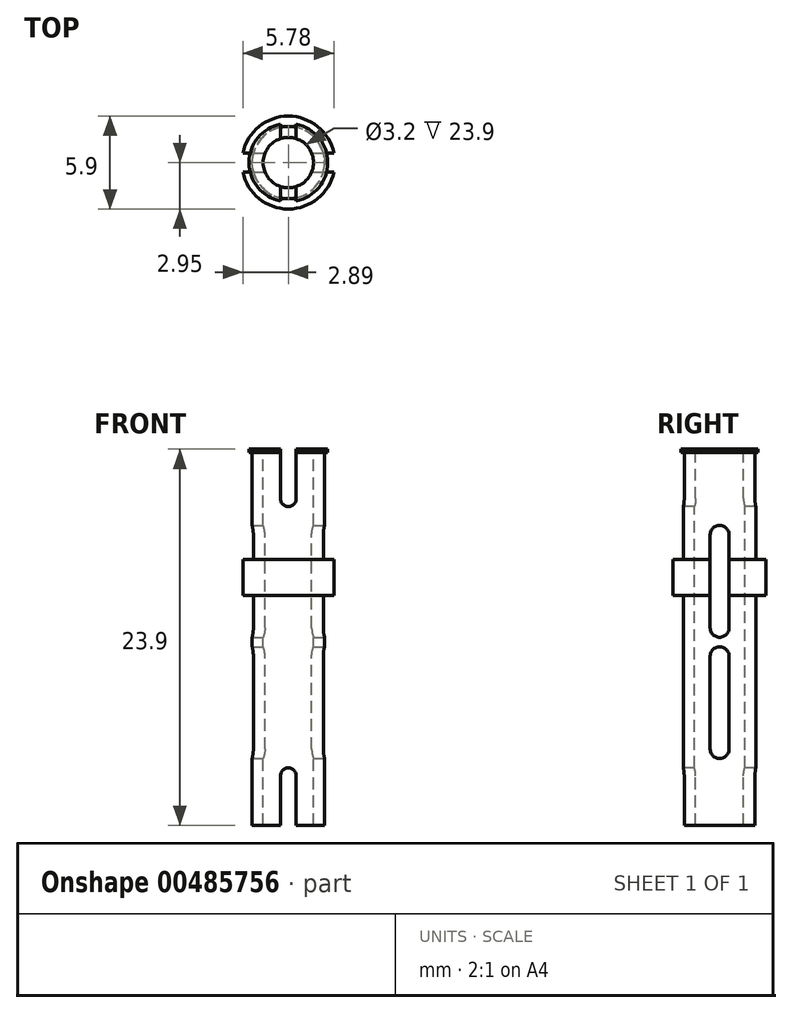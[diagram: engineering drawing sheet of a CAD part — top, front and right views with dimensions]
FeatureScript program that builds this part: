
annotation { "Feature Type Name" : "Feature", "Feature Type Description" : "" }
export const myFeature = defineFeature(function(context is Context, id is Id, definition is map)
    precondition{}
    {
        {
            var Q0;
            Q0=qCreatedBy(makeId("Top.planeOp"),FACE);
            var sketch = newSketch(context, id + "F0", { "sketchPlane" : qUnion([Q0])});
            skCircle(sketch, "E0", {"center": v(0, 0) * mm, "radius": 2.95 * mm});
            skSolve(sketch);
        }
        {
            var Q0;
            Q0 = qSketchRegion(id + "F0", true);
            extrude(context, id + "F1", {"entities" : qUnion([Q0]), "endBound" : BoundingType.SYMMETRIC, "depth" : 23.9 * mm, "offsetDistance" : 25 * mm});
        }
        {
            var Q0;
            Q0=makeQuery(id+"F1.opExtrude","CAP_FACE",FACE,{"disambiguationData":[OSD([sQuery(id+"F0.wireOp",EDGE,"E0")])],"isStart":false});
            var sketch = newSketch(context, id + "F2", { "sketchPlane" : qUnion([Q0])});
            skCircle(sketch, "E1", {"center": v(0, 0) * mm, "radius": 2.3 * mm});
            skSolve(sketch);
        }
        {
            var Q0;
            Q0=makeQuery(id+"F2.imprint","IMPRINT",FACE,{"disambiguationData":[TD([[makeQuery(id+"F2.imprint","IMPRINT",EDGE,{"derivedFrom":sQuery(id+"F2.wireOp",EDGE,"E1")}),-1.0]])]});
            extrude(context, id + "F3", {"entities" : qUnion([Q0]), "operationType" : NewBodyOperationType.REMOVE, "oppositeDirection" : true, "depth" : 7 * mm, "offsetDistance" : 25 * mm});
        }
        {
            var Q0;
            Q0=makeQuery(id+"F1.opExtrude","CAP_FACE",FACE,{"disambiguationData":[OSD([sQuery(id+"F0.wireOp",EDGE,"E0")])],"isStart":true});
            var sketch = newSketch(context, id + "F4", { "sketchPlane" : qUnion([Q0])});
            skCircle(sketch, "E2", {"center": v(0, 0) * mm, "radius": 2.3 * mm});
            skSolve(sketch);
        }
        {
            var Q0;
            Q0=makeQuery(id+"F4.imprint","IMPRINT",FACE,{"disambiguationData":[TD([[makeQuery(id+"F4.imprint","IMPRINT",EDGE,{"derivedFrom":sQuery(id+"F4.wireOp",EDGE,"E2")}),-1.0]])]});
            extrude(context, id + "F5", {"entities" : qUnion([Q0]), "operationType" : NewBodyOperationType.REMOVE, "oppositeDirection" : true, "depth" : 14.6 * mm, "offsetDistance" : 25 * mm});
        }
        {
            var Q0;
            Q0=makeQuery(id+"F1.opExtrude","CAP_FACE",FACE,{"disambiguationData":[OSD([sQuery(id+"F0.wireOp",EDGE,"E0")])],"isStart":false});
            var sketch = newSketch(context, id + "F6", { "sketchPlane" : qUnion([Q0])});
            skCircle(sketch, "E3", {"center": v(0, 0) * mm, "radius": 1.6 * mm});
            skSolve(sketch);
        }
        {
            var Q0;
            Q0 = qSketchRegion(id + "F6", true);
            extrude(context, id + "F7", {"entities" : qUnion([Q0]), "operationType" : NewBodyOperationType.REMOVE, "endBound" : BoundingType.THROUGH_ALL, "oppositeDirection" : true, "depth" : 25 * mm, "offsetDistance" : 25 * mm});
        }
        {
            var Q0;
            Q0=qCreatedBy(makeId("Front.planeOp"),FACE);
            var sketch = newSketch(context, id + "F8", { "sketchPlane" : qUnion([Q0])});
            skLineSegment(sketch, "E4.bottom", {"start": v(-0.5, 8.8) * mm, "end": v(0.5, 8.8) * mm});
            skLineSegment(sketch, "E4.top", {"start": v(-0.5, 11.95) * mm, "end": v(0.5, 11.95) * mm});
            skLineSegment(sketch, "E4.left", {"start": v(-0.5, 8.8) * mm, "end": v(-0.5, 11.95) * mm});
            skLineSegment(sketch, "E4.right", {"start": v(0.5, 8.8) * mm, "end": v(0.5, 11.95) * mm});
            skPoint(sketch, "E4.middle", {"position": v(0, 10.38) * mm});
            skCircle(sketch, "E5", {"center": v(0, 8.8) * mm, "radius": 0.5 * mm});
            skLineSegment(sketch, "E6.bottom", {"start": v(-0.5, -11.95) * mm, "end": v(0.5, -11.95) * mm});
            skLineSegment(sketch, "E6.top", {"start": v(-0.5, -8.8) * mm, "end": v(0.5, -8.8) * mm});
            skLineSegment(sketch, "E6.left", {"start": v(-0.5, -11.95) * mm, "end": v(-0.5, -8.8) * mm});
            skLineSegment(sketch, "E6.right", {"start": v(0.5, -11.95) * mm, "end": v(0.5, -8.8) * mm});
            skPoint(sketch, "E6.middle", {"position": v(0, -10.38) * mm});
            skCircle(sketch, "E7", {"center": v(0, -8.8) * mm, "radius": 0.5 * mm});
            skSolve(sketch);
        }
        {
            var Q0;
            Q0 = qSketchRegion(id + "F8", true);
            extrude(context, id + "F9", {"entities" : qUnion([Q0]), "operationType" : NewBodyOperationType.REMOVE, "endBound" : BoundingType.SYMMETRIC, "oppositeDirection" : true, "depth" : 25 * mm, "offsetDistance" : 25 * mm});
        }
        {
            var Q0;
            Q0=qCreatedBy(makeId("Front.planeOp"),FACE);
            var sketch = newSketch(context, id + "F10", { "sketchPlane" : qUnion([Q0])});
            skLineSegment(sketch, "E8.bottom", {"start": v(2.3, 11.95) * mm, "end": v(2.5, 11.95) * mm});
            skLineSegment(sketch, "E8.top", {"start": v(2.3, 11.75) * mm, "end": v(2.5, 11.75) * mm});
            skLineSegment(sketch, "E8.left", {"start": v(2.3, 11.95) * mm, "end": v(2.3, 11.75) * mm});
            skLineSegment(sketch, "E8.right", {"start": v(2.5, 11.95) * mm, "end": v(2.5, 11.75) * mm});
            skSolve(sketch);
        }
        {
            var Q0;
            Q0 = qSketchRegion(id + "F10", true);
            var Q1;
            Q1=makeQuery(id+"F3.boolean.opBoolean","COPY",FACE,{"derivedFrom":makeQuery(id+"F3.opExtrude","SWEPT_FACE",FACE,{"disambiguationData":[OSD([sQuery(id+"F2.wireOp",EDGE,"E1")])]})});
            revolve(context, id + "F11", {"operationType" : NewBodyOperationType.ADD, "entities" : qUnion([Q0]), "axis" : qUnion([Q1]), "revolveType" : RevolveType.FULL});
        }
        {
            var Q0;
            Q0 = qSketchRegion(id + "F8", true);
            extrude(context, id + "F12", {"entities" : qUnion([Q0]), "operationType" : NewBodyOperationType.REMOVE, "endBound" : BoundingType.SYMMETRIC, "depth" : 25 * mm, "offsetDistance" : 25 * mm});
        }
        {
            var Q0;
            Q0 = qSketchRegion(id + "F8", true);
            extrude(context, id + "F13", {"entities" : qUnion([Q0]), "operationType" : NewBodyOperationType.REMOVE, "endBound" : BoundingType.SYMMETRIC, "oppositeDirection" : true, "depth" : 25 * mm, "offsetDistance" : 25 * mm});
        }
        {
            var Q0;
            Q0=qCreatedBy(makeId("Right.planeOp"),FACE);
            var sketch = newSketch(context, id + "F14", { "sketchPlane" : qUnion([Q0])});
            skLineSegment(sketch, "E9.bottom", {"start": v(0.6, 0.6) * mm, "end": v(-0.6, 0.6) * mm});
            skLineSegment(sketch, "E9.top", {"start": v(0.6, 6.5) * mm, "end": v(-0.6, 6.5) * mm});
            skLineSegment(sketch, "E9.left", {"start": v(0.6, 0.6) * mm, "end": v(0.6, 6.5) * mm});
            skLineSegment(sketch, "E9.right", {"start": v(-0.6, 0.6) * mm, "end": v(-0.6, 6.5) * mm});
            skPoint(sketch, "E9.middle", {"position": v(0, 3.55) * mm});
            skLineSegment(sketch, "E10.bottom", {"start": v(0.6, -7.1) * mm, "end": v(-0.6, -7.1) * mm});
            skLineSegment(sketch, "E10.top", {"start": v(0.6, -1.2) * mm, "end": v(-0.6, -1.2) * mm});
            skLineSegment(sketch, "E10.left", {"start": v(0.6, -7.1) * mm, "end": v(0.6, -1.2) * mm});
            skLineSegment(sketch, "E10.right", {"start": v(-0.6, -7.1) * mm, "end": v(-0.6, -1.2) * mm});
            skPoint(sketch, "E10.middle", {"position": v(0, -4.15) * mm});
            skCircle(sketch, "E11", {"center": v(0, 0.6) * mm, "radius": 0.6 * mm});
            skCircle(sketch, "E12", {"center": v(0, -1.2) * mm, "radius": 0.6 * mm});
            skCircle(sketch, "E13", {"center": v(0, 6.5) * mm, "radius": 0.6 * mm});
            skCircle(sketch, "E14", {"center": v(0, -7.1) * mm, "radius": 0.6 * mm});
            skSolve(sketch);
        }
        {
            var Q0;
            Q0 = qSketchRegion(id + "F14", true);
            extrude(context, id + "F15", {"entities" : qUnion([Q0]), "operationType" : NewBodyOperationType.REMOVE, "endBound" : BoundingType.SYMMETRIC, "oppositeDirection" : true, "depth" : 25 * mm, "offsetDistance" : 25 * mm});
        }
    });
